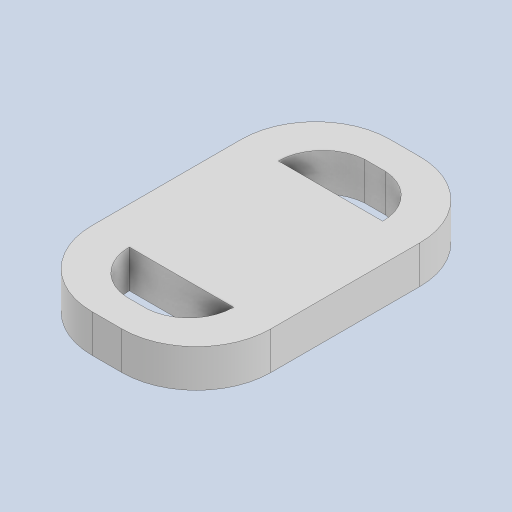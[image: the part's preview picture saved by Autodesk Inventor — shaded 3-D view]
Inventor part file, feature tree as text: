
AUTODESK INVENTOR PART (.ipt)
format: ipt  version: 2024 (Build 280153000, 153)  size: 125,440 bytes
history: native  units: mm
features: other x1, extrude x1, sketch x1
ambient origin geometry x8: Origin, YZ Plane, XZ Plane, XY Plane, X Axis, Y Axis, Z Axis, Center Point
bodies: Body1 (feature_tree)
feature tree (3):
  other  "Sólido1"
  extrude  "Extrusión1"  Depth=50.0mm
  sketch  "Boceto1"  dims[d0=120.0mm d2=50.0mm d3=200.0mm d5=70.0mm d6=30.0mm d7=25.4mm d8=0.0mm]
